# Revit family: Air_Curtain-Ambient-Berner_International-AHC10
name_source: partatom
category: Mechanical Equipment
revit_build: Autodesk Revit 2015 (Build: 20140606_1530(x64)
units: mm (PartAtom-declared; Revit-internal decimal feet)

## types (1)
- AHC10-1036A
    Air Volume = 0 CFM
    Amps per Circuit = 0 A
    Assembly Code = D3090400
    Average Outlet Velocity = 0 FPM
    Berner AHC10 Conduit Radius = 0' - 0 1/4"
    Breaker Rating per Circuit = 0 A
    DBL = Yes
    Description = Ambient Heated Air Door Unit
    Environmental Separation = Yes
    Filter = No
    Hertz = 60 Hz
    Inlet Screen = Aluminum Perforated Metal  - Berner International -  Satin -  Inlet Screen
    Insect Control = No
    Manufacturer = Berner International Corp.
    Maximum Velocity at Nozzle = 0 FPM
    Model = No Model Specified - See Use Instructions
    Motor Volts = 0 V
    Motors per Unit = 0
    Mounting Width C = 2' - 3"
    NVW2 = 2' - 9 5/32"
    Net Weight = 0.00 kip
    Nozzle Width = 8' - 2 1/2"
    Outlet Velocity Uniform (%) = 0.00%
    Phase = 1
    Power Rating = 0 W
    Product data url = https://bimobject.com
    SGL = No
    Show Service Clearance = Yes
    TRP = No
    Type Catalog Loaded = Not loaded by Type Catalog - Parameters Invalid
    URL = http://www.berner.com
    Unit Color = Anodized Aluminum - Berner International - Clear Satin
    Unit Height = 1' - 0 1/4"
    Unit Width = 8' - 3 1/2"

## geometry (parser evidence)
native form markers: Blend x14, Sweep x5
no freeform markers — native parametric forms only
